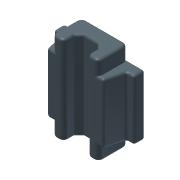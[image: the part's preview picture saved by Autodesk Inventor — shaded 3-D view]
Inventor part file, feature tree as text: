
AUTODESK INVENTOR PART (.ipt)
format: ipt  version: 2014 (Build 180170000, 170)  size: 256,000 bytes
history: native  units: mm
features: extrude x3, fillet x3, sketch x3, chamfer x1, mirror x1, plane x1
ambient origin geometry x8: Origin, YZ Plane, XZ Plane, XY Plane, X Axis, Y Axis, Z Axis, Center Point
bodies: Solid1 (feature_tree)
feature tree (12):
  extrude  "Extrusion1"  Depth=19.0mm
  chamfer  "Chamfer1"  Distance=56.9mm
  fillet  "Fillet1"  Radius=3.0mm
  fillet  "Fillet2"  Radius=3.0mm
  extrude  "Extrusion2"  Depth=1.5mm
  fillet  "Fillet3"  Radius=7.0mm
  mirror  "Mirror1"
  extrude  "Extrusion3"  Depth=5.0mm
  sketch  "Sketch1"  dims[d0=15.0mm d1=19.0mm]
  sketch  "Sketch2"  dims[d2=30.0mm]
  plane  "Work Plane1"
  sketch  "Sketch3"  dims[d3=10.0mm d4=56.9mm d5=0.0mm d6=3.0mm d7=2.0mm d8=45.0deg d9=3.0mm d10=1.5mm d11=7.0mm d12=26.0mm d13=6.0mm d14=5.0mm d15=38.7mm d16=0.0mm d17=1.5mm d18=26.0mm d19=41.0mm d20=4.0mm d21=5.0mm d22=0.0mm]
